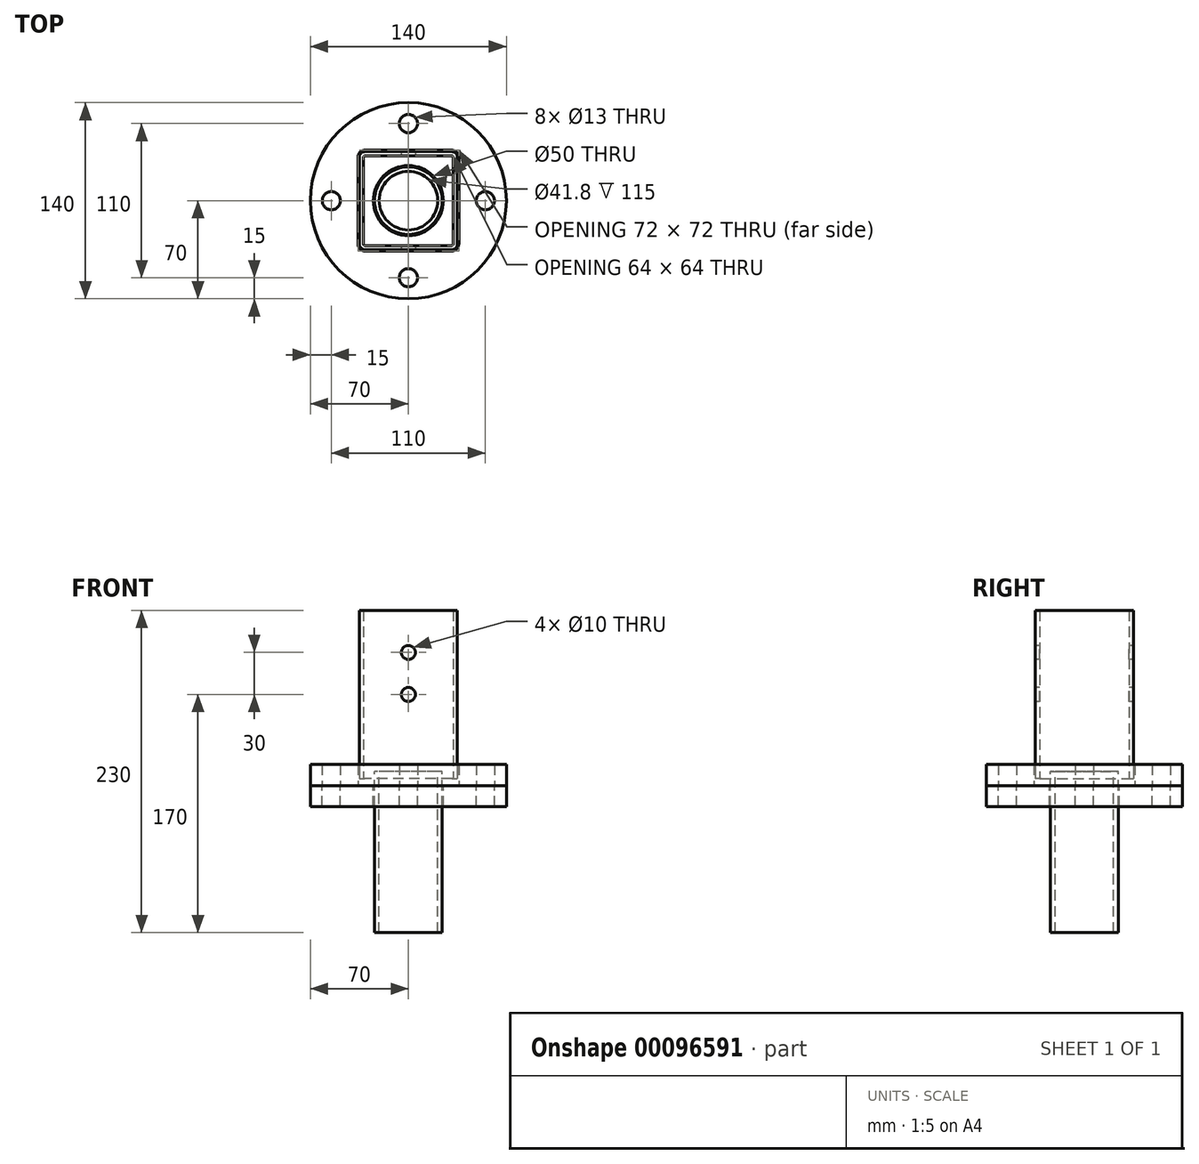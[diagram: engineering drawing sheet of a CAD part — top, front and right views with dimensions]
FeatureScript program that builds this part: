
annotation { "Feature Type Name" : "Feature", "Feature Type Description" : "" }
export const myFeature = defineFeature(function(context is Context, id is Id, definition is map)
    precondition{}
    {
        {
            var Q0;
            Q0=qCreatedBy(makeId("Top.planeOp"),FACE);
            var sketch = newSketch(context, id + "F0", { "sketchPlane" : qUnion([Q0])});
            skLineSegment(sketch, "E0.bottom", {"start": v(31, -35) * mm, "end": v(-31, -35) * mm});
            skLineSegment(sketch, "E0.top", {"start": v(31, 35) * mm, "end": v(-31, 35) * mm});
            skLineSegment(sketch, "E0.left", {"start": v(35, -31) * mm, "end": v(35, 31) * mm});
            skLineSegment(sketch, "E0.right", {"start": v(-35, -31) * mm, "end": v(-35, 31) * mm});
            skPoint(sketch, "E0.middle", {"position": v(0, 0) * mm});
            skPoint(sketch, "E1.visualSharp", {"position": v(-35, 35) * mm});
            skArc(sketch, "E1.filletArc", {"start": v(-31, 35) * mm, "mid": v(-33.83, 33.83) * mm, "end": v(-35, 31) * mm});
            skPoint(sketch, "E2.visualSharp", {"position": v(-35, -35) * mm});
            skArc(sketch, "E2.filletArc", {"start": v(-35, -31) * mm, "mid": v(-33.83, -33.83) * mm, "end": v(-31, -35) * mm});
            skPoint(sketch, "E3.visualSharp", {"position": v(35, -35) * mm});
            skArc(sketch, "E3.filletArc", {"start": v(31, -35) * mm, "mid": v(33.83, -33.83) * mm, "end": v(35, -31) * mm});
            skPoint(sketch, "E4.visualSharp", {"position": v(35, 35) * mm});
            skArc(sketch, "E4.filletArc", {"start": v(35, 31) * mm, "mid": v(33.83, 33.83) * mm, "end": v(31, 35) * mm});
            skArc(sketch, "E5.0", {"start": v(32, 31) * mm, "mid": v(31.7, 31.7) * mm, "end": v(31, 32) * mm});
            skLineSegment(sketch, "E5.1", {"start": v(32, -31) * mm, "end": v(32, 31) * mm});
            skLineSegment(sketch, "E5.2", {"start": v(31, 32) * mm, "end": v(-31, 32) * mm});
            skArc(sketch, "E5.3", {"start": v(31, -32) * mm, "mid": v(31.7, -31.7) * mm, "end": v(32, -31) * mm});
            skArc(sketch, "E5.4", {"start": v(-31, 32) * mm, "mid": v(-31.7, 31.7) * mm, "end": v(-32, 31) * mm});
            skLineSegment(sketch, "E5.5", {"start": v(-32, -31) * mm, "end": v(-32, 31) * mm});
            skArc(sketch, "E5.6", {"start": v(-32, -31) * mm, "mid": v(-31.7, -31.7) * mm, "end": v(-31, -32) * mm});
            skLineSegment(sketch, "E5.7", {"start": v(31, -32) * mm, "end": v(-31, -32) * mm});
            skSolve(sketch);
        }
        {
            var Q0;
            Q0=makeQuery(id+"F0.imprint","IMPRINT",FACE,{"disambiguationData":[TD([[makeQuery(id+"F0.imprint","IMPRINT",EDGE,{"derivedFrom":sQuery(id+"F0.wireOp",EDGE,"E0.bottom")}),-1.0]])]});
            var Q1;
            Q1=sQuery(id+"F0.wireOp",EDGE,"E0.right");
            extrude(context, id + "F1", {"entities" : qUnion([Q0]), "surfaceEntities" : qUnion([Q1]), "depth" : 120 * mm});
        }
        {
            var Q0;
            Q0=makeQuery(id+"F1.opExtrude","SWEPT_FACE",FACE,{"disambiguationData":[OSD([sQuery(id+"F0.wireOp",EDGE,"E0.bottom")])]});
            var sketch = newSketch(context, id + "F2", { "sketchPlane" : qUnion([Q0])});
            skPoint(sketch, "E6", {"position": v(0, 60) * mm});
            skPoint(sketch, "E7", {"position": v(0, 90) * mm});
            skSolve(sketch);
        }
        {
            var Q0;
            Q0=sQuery(id+"F2.wireOp",VERTEX,"E7");
            var Q1;
            Q1=sQuery(id+"F2.wireOp",VERTEX,"E6");
            var Q2;
            Q2=makeQuery(id+"F1.opExtrude","SWEPT_BODY",BODY,{"disambiguationData":[OSD([sQuery(id+"F0.wireOp",EDGE,"E0.bottom"),sQuery(id+"F0.wireOp",EDGE,"E0.top"),sQuery(id+"F0.wireOp",EDGE,"E0.left"),sQuery(id+"F0.wireOp",EDGE,"E0.right"),sQuery(id+"F0.wireOp",EDGE,"E1.filletArc"),sQuery(id+"F0.wireOp",EDGE,"E2.filletArc"),sQuery(id+"F0.wireOp",EDGE,"E3.filletArc"),sQuery(id+"F0.wireOp",EDGE,"E4.filletArc"),sQuery(id+"F0.wireOp",EDGE,"E5.0"),sQuery(id+"F0.wireOp",EDGE,"E5.1"),sQuery(id+"F0.wireOp",EDGE,"E5.2"),sQuery(id+"F0.wireOp",EDGE,"E5.3"),sQuery(id+"F0.wireOp",EDGE,"E5.4"),sQuery(id+"F0.wireOp",EDGE,"E5.5"),sQuery(id+"F0.wireOp",EDGE,"E5.6"),sQuery(id+"F0.wireOp",EDGE,"E5.7")])]});
            hole(context, id + "F3", {"style" : HoleStyle.SIMPLE, "endStyle" : HoleEndStyle.THROUGH, "holeDiameter" : 10 * mm, "locations" : qUnion([Q0, Q1]), "scope" : qUnion([Q2]), "isTappedThrough" : true});
        }
        {
            var Q0;
            Q0=qCreatedBy(makeId("Top.planeOp"),FACE);
            cPlane(context, id + "F4", {"entities" : qUnion([Q0]), "cplaneType" : CPlaneType.OFFSET, "offset" : 10 * mm, "oppositeDirection" : true, "width" : 150 * mm, "height" : 150 * mm});
        }
        {
            var Q0;
            Q0=qCreatedBy(id+"F4.planeOp",FACE);
            var sketch = newSketch(context, id + "F5", { "sketchPlane" : qUnion([Q0])});
            skCircle(sketch, "E8", {"center": v(0, 0) * mm, "radius": 24.15 * mm});
            skCircle(sketch, "E9", {"center": v(0, 0) * mm, "radius": 20.9 * mm});
            skSolve(sketch);
        }
        {
            var Q0;
            Q0 = qSketchRegion(id + "F5", true);
            extrude(context, id + "F6", {"entities" : qUnion([Q0]), "oppositeDirection" : true, "depth" : 100 * mm, "hasSecondDirection" : true, "secondDirectionOppositeDirection" : false, "secondDirectionDepth" : 15 * mm});
        }
        {
            var Q0;
            Q0=qCreatedBy(makeId("Top.planeOp"),FACE);
            var sketch = newSketch(context, id + "F7", { "sketchPlane" : qUnion([Q0])});
            skCircle(sketch, "E10", {"center": v(0, 0) * mm, "radius": 70 * mm});
            skCircle(sketch, "E11", {"center": v(0, 0) * mm, "radius": 55 * mm, "construction": true});
            skCircle(sketch, "E12", {"center": v(-55, 0) * mm, "radius": 6.5 * mm});
            skCircle(sketch, "E13", {"center": v(0, 55) * mm, "radius": 6.5 * mm});
            skCircle(sketch, "E14", {"center": v(55, 0) * mm, "radius": 6.5 * mm});
            skCircle(sketch, "E15", {"center": v(0, -55) * mm, "radius": 6.5 * mm});
            skArc(sketch, "E16.0", {"start": v(36, 31) * mm, "mid": v(34.54, 34.54) * mm, "end": v(31, 36) * mm});
            skLineSegment(sketch, "E16.1", {"start": v(36, -31) * mm, "end": v(36, 31) * mm});
            skLineSegment(sketch, "E16.2", {"start": v(31, 36) * mm, "end": v(-31, 36) * mm});
            skArc(sketch, "E16.3", {"start": v(31, -36) * mm, "mid": v(34.54, -34.54) * mm, "end": v(36, -31) * mm});
            skArc(sketch, "E16.4", {"start": v(-31, 36) * mm, "mid": v(-34.54, 34.54) * mm, "end": v(-36, 31) * mm});
            skLineSegment(sketch, "E16.5", {"start": v(-36, -31) * mm, "end": v(-36, 31) * mm});
            skArc(sketch, "E16.6", {"start": v(-36, -31) * mm, "mid": v(-34.54, -34.54) * mm, "end": v(-31, -36) * mm});
            skLineSegment(sketch, "E16.7", {"start": v(31, -36) * mm, "end": v(-31, -36) * mm});
            skSolve(sketch);
        }
        {
            var Q0;
            Q0 = qSketchRegion(id + "F7", true);
            extrude(context, id + "F8", {"entities" : qUnion([Q0]), "depth" : 10 * mm, "hasSecondDirection" : true, "secondDirectionOppositeDirection" : true, "secondDirectionDepth" : 5 * mm});
        }
        {
            var Q0;
            Q0=qCreatedBy(id+"F4.planeOp",FACE);
            var sketch = newSketch(context, id + "F9", { "sketchPlane" : qUnion([Q0])});
            skCircle(sketch, "E17.0", {"center": v(-55, 0) * mm, "radius": 6.5 * mm});
            skCircle(sketch, "E18.0", {"center": v(0, 55) * mm, "radius": 6.5 * mm});
            skCircle(sketch, "E19.0", {"center": v(55, 0) * mm, "radius": 6.5 * mm});
            skCircle(sketch, "E20.0", {"center": v(0, 0) * mm, "radius": 70 * mm});
            skCircle(sketch, "E21.0", {"center": v(0, -55) * mm, "radius": 6.5 * mm});
            skCircle(sketch, "E22", {"center": v(0, 0) * mm, "radius": 25 * mm});
            skSolve(sketch);
        }
        {
            var Q0;
            Q0 = qSketchRegion(id + "F9", true);
            extrude(context, id + "F10", {"entities" : qUnion([Q0]), "oppositeDirection" : true, "depth" : 10 * mm, "hasSecondDirection" : true, "secondDirectionOppositeDirection" : false, "secondDirectionDepth" : 5 * mm});
        }
    });
